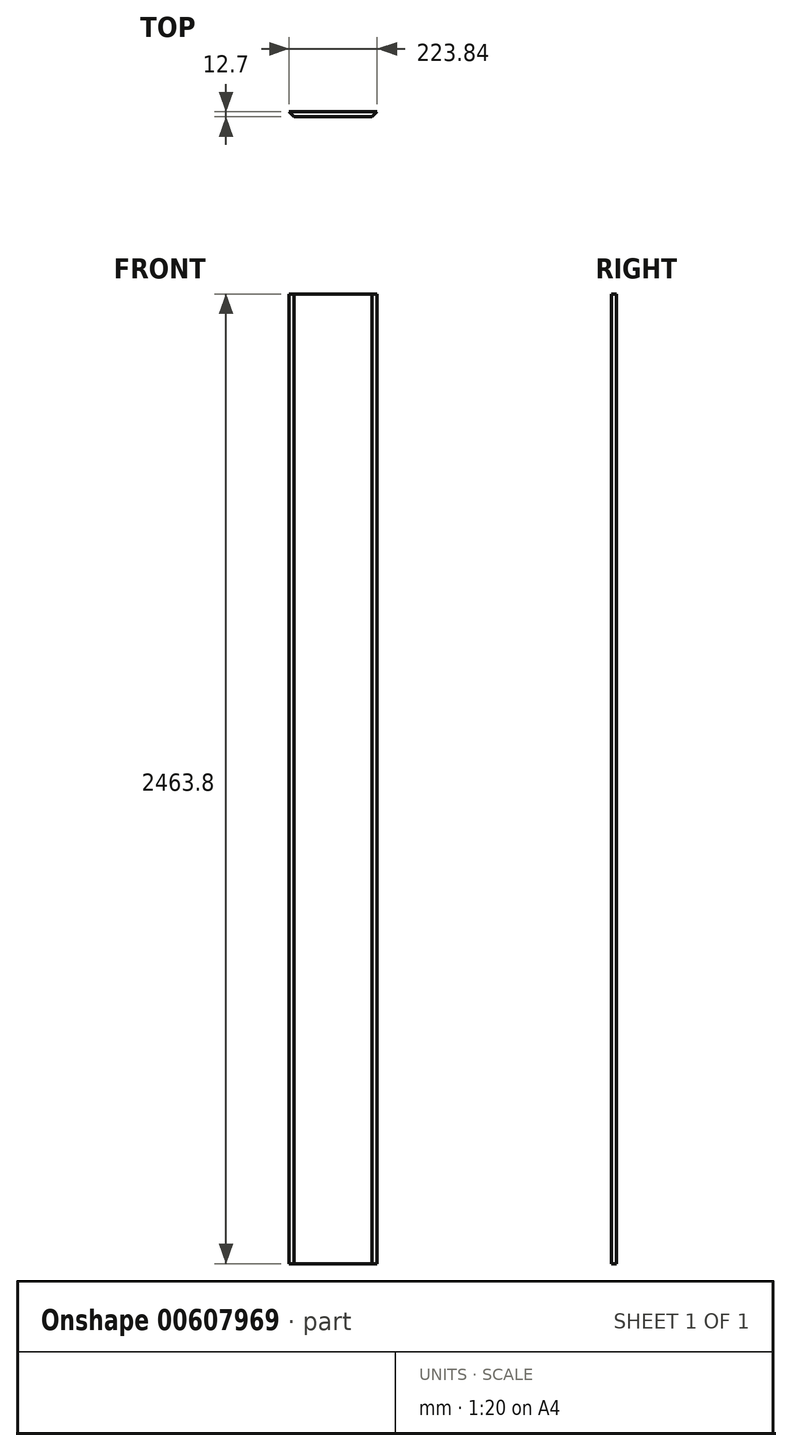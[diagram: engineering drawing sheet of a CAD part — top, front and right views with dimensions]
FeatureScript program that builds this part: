
annotation { "Feature Type Name" : "Feature", "Feature Type Description" : "" }
export const myFeature = defineFeature(function(context is Context, id is Id, definition is map)
    precondition{}
    {
        {
            var Q0;
            Q0=qCreatedBy(makeId("Top.planeOp"),FACE);
            var sketch = newSketch(context, id + "F0", { "sketchPlane" : qUnion([Q0])});
            skLineSegment(sketch, "E0.bottom", {"start": v(99.22, -6.35) * mm, "end": v(-99.22, -6.35) * mm});
            skLineSegment(sketch, "E0.top", {"start": v(99.22, 6.35) * mm, "end": v(-99.22, 6.35) * mm});
            skPoint(sketch, "E0.middle", {"position": v(0, 0) * mm});
            skLineSegment(sketch, "E1", {"start": v(99.22, -6.35) * mm, "end": v(111.92, 6.35) * mm});
            skLineSegment(sketch, "E2", {"start": v(111.92, 6.35) * mm, "end": v(99.22, 6.35) * mm});
            skLineSegment(sketch, "E3.MirrorCS", {"start": v(-99.22, -6.35) * mm, "end": v(-111.92, 6.35) * mm});
            skLineSegment(sketch, "E4.MirrorCS", {"start": v(-111.92, 6.35) * mm, "end": v(-99.22, 6.35) * mm});
            skSolve(sketch);
        }
        {
            var Q0;
            Q0=makeQuery(id+"F0.imprint","IMPRINT",FACE,{"disambiguationData":[TD([[makeQuery(id+"F0.imprint","IMPRINT",EDGE,{"derivedFrom":sQuery(id+"F0.wireOp",EDGE,"E0.bottom")}),-1.0]])]});
            extrude(context, id + "F1", {"entities" : qUnion([Q0]), "endBound" : BoundingType.SYMMETRIC, "depth" : 2463.8 * mm, "offsetDistance" : 25.4 * mm});
        }
    });
